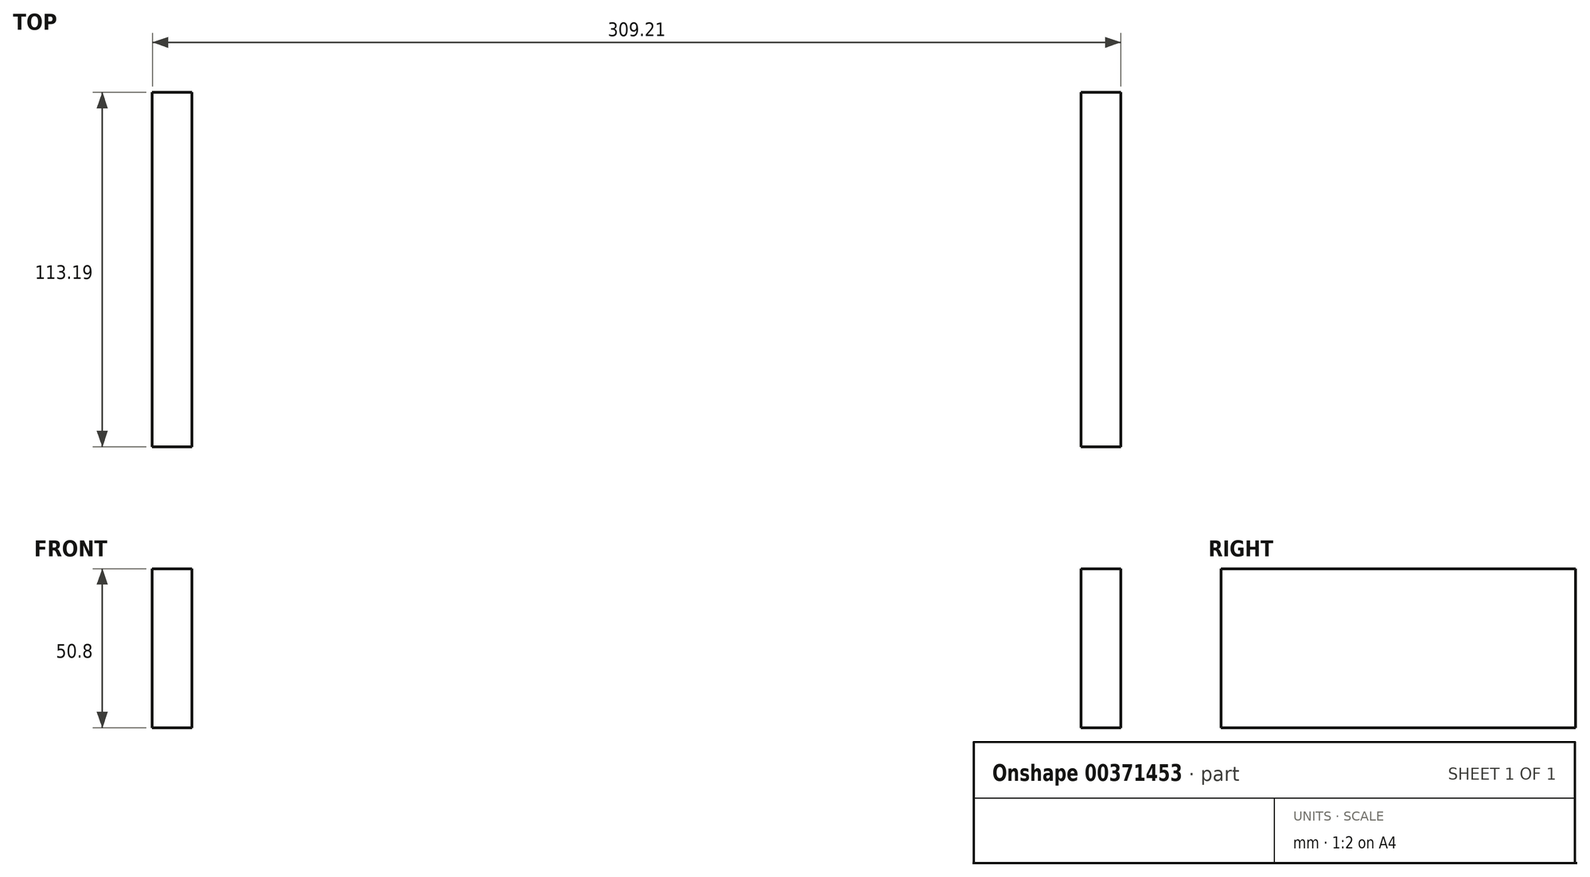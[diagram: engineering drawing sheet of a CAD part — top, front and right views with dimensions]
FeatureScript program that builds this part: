
annotation { "Feature Type Name" : "Feature", "Feature Type Description" : "" }
export const myFeature = defineFeature(function(context is Context, id is Id, definition is map)
    precondition{}
    {
        {
            var Q0;
            Q0=qCreatedBy(makeId("Top.planeOp"),FACE);
            var sketch = newSketch(context, id + "F0", { "sketchPlane" : qUnion([Q0])});
            skLineSegment(sketch, "E0.bottom", {"start": v(143, 54.6) * mm, "end": v(-166.21, 54.6) * mm});
            skLineSegment(sketch, "E0.top", {"start": v(143, -71.3) * mm, "end": v(-166.21, -71.3) * mm});
            skLineSegment(sketch, "E0.left", {"start": v(143, 54.6) * mm, "end": v(143, -71.3) * mm});
            skLineSegment(sketch, "E0.right", {"start": v(-166.21, 54.6) * mm, "end": v(-166.21, -71.3) * mm});
            skPoint(sketch, "E0.middle", {"position": v(-11.6, -8.36) * mm});
            skLineSegment(sketch, "E1.bottom", {"start": v(-166.21, 54.6) * mm, "end": v(143, 54.6) * mm});
            skLineSegment(sketch, "E1.top", {"start": v(-166.21, 41.9) * mm, "end": v(143, 41.9) * mm});
            skLineSegment(sketch, "E1.left", {"start": v(-166.21, 54.6) * mm, "end": v(-166.21, 41.9) * mm});
            skLineSegment(sketch, "E1.right", {"start": v(143, 54.6) * mm, "end": v(143, 41.9) * mm});
            skLineSegment(sketch, "E2.bottom", {"start": v(130.3, 41.9) * mm, "end": v(143, 41.9) * mm});
            skLineSegment(sketch, "E2.top", {"start": v(130.3, -71.3) * mm, "end": v(143, -71.3) * mm});
            skLineSegment(sketch, "E2.left", {"start": v(130.3, 41.9) * mm, "end": v(130.3, -71.3) * mm});
            skLineSegment(sketch, "E2.right", {"start": v(143, 41.9) * mm, "end": v(143, -71.3) * mm});
            skLineSegment(sketch, "E3.bottom", {"start": v(-153.51, 41.9) * mm, "end": v(-166.21, 41.9) * mm});
            skLineSegment(sketch, "E3.top", {"start": v(-153.51, -71.3) * mm, "end": v(-166.21, -71.3) * mm});
            skLineSegment(sketch, "E3.left", {"start": v(-153.51, 41.9) * mm, "end": v(-153.51, -71.3) * mm});
            skLineSegment(sketch, "E3.right", {"start": v(-166.21, 41.9) * mm, "end": v(-166.21, -71.3) * mm});
            skCircle(sketch, "E4", {"center": v(-6.16, -18.3) * mm, "radius": 33.02 * mm});
            skCircle(sketch, "E5", {"center": v(-106.03, -18.3) * mm, "radius": 33.02 * mm});
            skCircle(sketch, "E6", {"center": v(87.8, -18.3) * mm, "radius": 33.02 * mm});
            skSolve(sketch);
        }
        {
            var Q0;
            Q0=makeQuery(id+"F0.imprint","IMPRINT",FACE,{"disambiguationData":[TD([[makeQuery(id+"F0.imprint","IMPRINT",EDGE,{"derivedFrom":sQuery(id+"F0.wireOp",EDGE,"E0.top")}),-1.0]])]});
            extrude(context, id + "F1", {"entities" : qUnion([Q0]), "depth" : -50.8 * mm});
        }
    });
